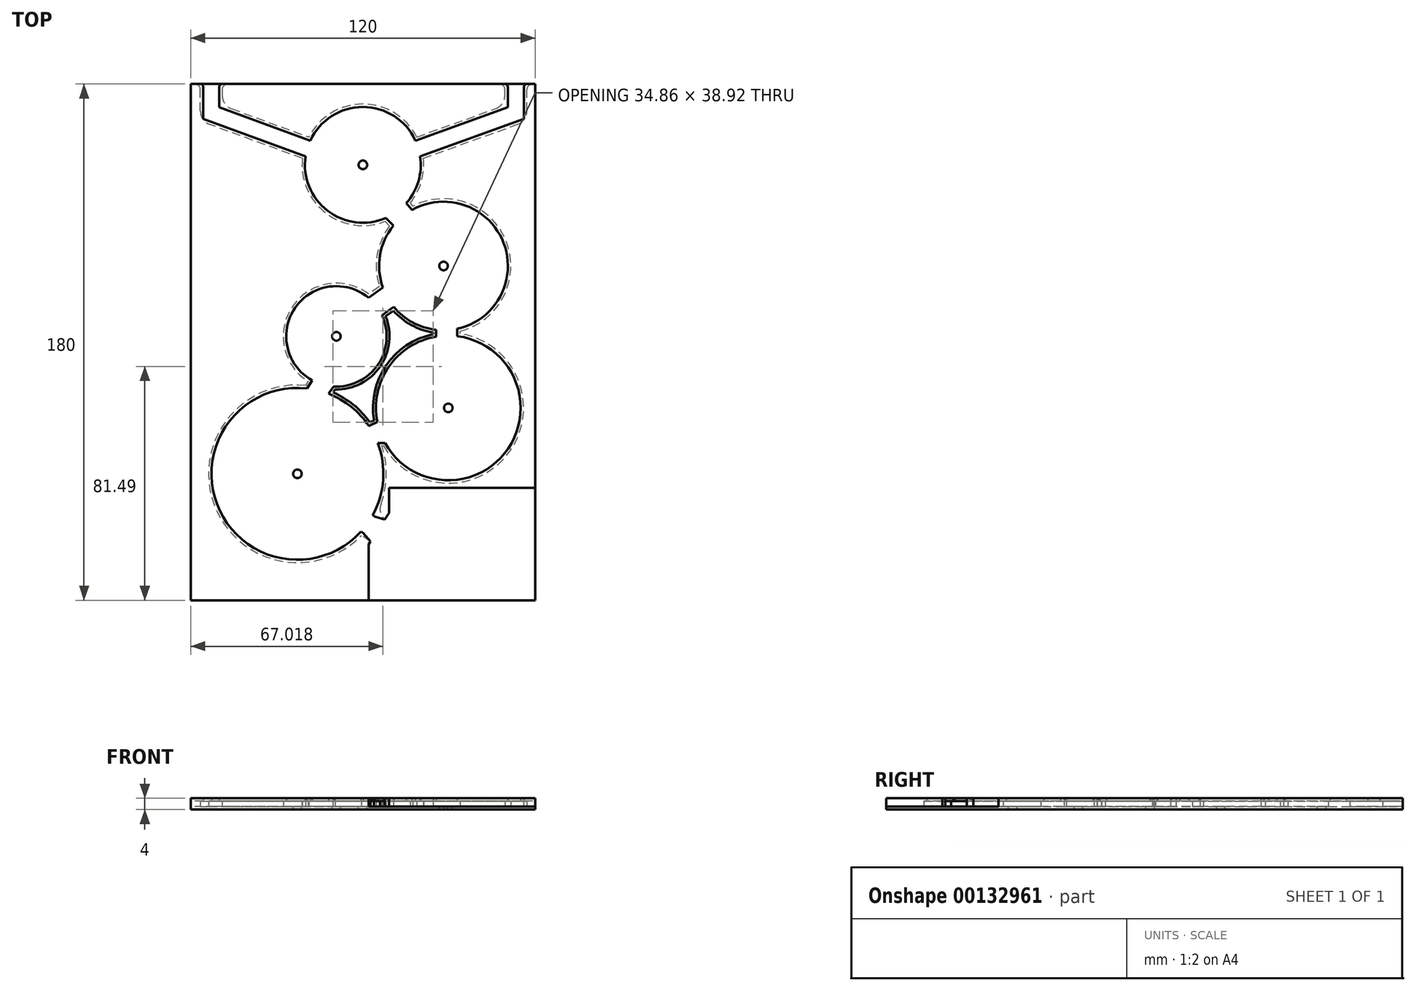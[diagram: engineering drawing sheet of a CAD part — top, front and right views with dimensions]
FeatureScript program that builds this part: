
annotation { "Feature Type Name" : "Feature", "Feature Type Description" : "" }
export const myFeature = defineFeature(function(context is Context, id is Id, definition is map)
    precondition{}
    {
        {
            var Q0;
            Q0=qCreatedBy(makeId("Top.planeOp"),FACE);
            var sketch = newSketch(context, id + "F0", { "sketchPlane" : qUnion([Q0])});
            skLineSegment(sketch, "E0.bottom", {"start": v(60, -90) * mm, "end": v(-60, -90) * mm});
            skLineSegment(sketch, "E0.top", {"start": v(60, 90) * mm, "end": v(-60, 90) * mm});
            skLineSegment(sketch, "E0.left", {"start": v(60, -90) * mm, "end": v(60, 90) * mm});
            skLineSegment(sketch, "E0.right", {"start": v(-60, -90) * mm, "end": v(-60, 90) * mm});
            skPoint(sketch, "E0.middle", {"position": v(0, 0) * mm});
            skSolve(sketch);
        }
        {
            var Q0;
            Q0 = qSketchRegion(id + "F0", true);
            extrude(context, id + "F1", {"entities" : qUnion([Q0]), "depth" : 1 * mm});
        }
        {
            var Q0;
            Q0=makeQuery(id+"F1.opExtrude","CAP_FACE",FACE,{"disambiguationData":[OSD([sQuery(id+"F0.wireOp",EDGE,"E0.bottom"),sQuery(id+"F0.wireOp",EDGE,"E0.top"),sQuery(id+"F0.wireOp",EDGE,"E0.left"),sQuery(id+"F0.wireOp",EDGE,"E0.right")])],"isStart":false});
            var sketch = newSketch(context, id + "F2", { "sketchPlane" : qUnion([Q0])});
            skArc(sketch, "E1", {"start": v(9.31, 40.56) * mm, "mid": v(4.98, 30.41) * mm, "end": v(5.77, 19.41) * mm});
            skArc(sketch, "E2", {"start": v(2, 16.73) * mm, "mid": v(-24.42, 12.56) * mm, "end": v(-19.08, -13.65) * mm});
            skArc(sketch, "E3", {"start": v(-19.98, -15.08) * mm, "mid": v(-51.81, -56.71) * mm, "end": v(-0.51, -67.4) * mm});
            skArc(sketch, "E4", {"start": v(24.45, 2.73) * mm, "mid": v(8.12, -8.13) * mm, "end": v(3.9, -27.29) * mm});
            skArc(sketch, "E5", {"start": v(16.45, 48.47) * mm, "mid": v(-12.5, 78.9) * mm, "end": v(7.75, 42.1) * mm});
            skLineSegment(sketch, "E6.bottom", {"start": v(-60, 90) * mm, "end": v(60, 90) * mm});
            skLineSegment(sketch, "E6.top", {"start": v(-60, -90) * mm, "end": v(60, -90) * mm});
            skLineSegment(sketch, "E6.left", {"start": v(-60, 90) * mm, "end": v(-60, -90) * mm});
            skLineSegment(sketch, "E6.right", {"start": v(60, 90) * mm, "end": v(60, -90) * mm});
            skLineSegment(sketch, "E7", {"start": v(7.75, 42.1) * mm, "end": v(9.31, 40.56) * mm});
            skLineSegment(sketch, "E8", {"start": v(16.45, 48.47) * mm, "end": v(17.36, 47.38) * mm});
            skLineSegment(sketch, "E9", {"start": v(5.77, 19.41) * mm, "end": v(2, 16.73) * mm});
            skLineSegment(sketch, "E10", {"start": v(10.6, 10.95) * mm, "end": v(7.9, 9.04) * mm});
            skArc(sketch, "E11.trimOffspring", {"start": v(10.6, 10.95) * mm, "mid": v(16.87, 5.97) * mm, "end": v(24.45, 3.4) * mm});
            skLineSegment(sketch, "E12", {"start": v(24.45, 2.73) * mm, "end": v(24.45, 3.4) * mm});
            skLineSegment(sketch, "E13", {"start": v(33.93, 2.94) * mm, "end": v(33.93, 3.84) * mm});
            skArc(sketch, "E14.trimOffspring", {"start": v(33.93, 3.84) * mm, "mid": v(50, 34.88) * mm, "end": v(17.36, 47.38) * mm});
            skLineSegment(sketch, "E15", {"start": v(-19.08, -13.65) * mm, "end": v(-19.98, -15.08) * mm});
            skLineSegment(sketch, "E16", {"start": v(-10.4, -17.54) * mm, "end": v(-9.65, -16.5) * mm});
            skArc(sketch, "E17.trimOffspring", {"start": v(-9.65, -16.5) * mm, "mid": v(6.03, -8.47) * mm, "end": v(7.9, 9.04) * mm});
            skLineSegment(sketch, "E18", {"start": v(2.43, -27.97) * mm, "end": v(3.9, -27.29) * mm});
            skLineSegment(sketch, "E19", {"start": v(6.58, -36.13) * mm, "end": v(7.09, -36.13) * mm});
            skArc(sketch, "E20.trimOffspring", {"start": v(7.09, -36.13) * mm, "mid": v(51.38, -37.8) * mm, "end": v(33.93, 2.94) * mm});
            skArc(sketch, "E21.trimOffspring", {"start": v(2.43, -27.97) * mm, "mid": v(-3.28, -21.88) * mm, "end": v(-10.4, -17.54) * mm});
            skLineSegment(sketch, "E22.bottom", {"start": v(60, -90) * mm, "end": v(9.07, -90) * mm});
            skLineSegment(sketch, "E22.top", {"start": v(60, -50.87) * mm, "end": v(9.07, -50.87) * mm});
            skLineSegment(sketch, "E22.left", {"start": v(60, -90) * mm, "end": v(60, -50.87) * mm});
            skLineSegment(sketch, "E23.bottom", {"start": v(1.97, -90) * mm, "end": v(9.07, -90) * mm});
            skLineSegment(sketch, "E23.left", {"start": v(1.97, -90) * mm, "end": v(1.97, -70.43) * mm});
            skLineSegment(sketch, "E24", {"start": v(1.97, -70.43) * mm, "end": v(2.62, -69.44) * mm});
            skLineSegment(sketch, "E25.trimOffspring", {"start": v(9.07, -59.55) * mm, "end": v(9.07, -50.87) * mm});
            skLineSegment(sketch, "E26", {"start": v(7.56, -61.87) * mm, "end": v(4.75, -60.04) * mm});
            skLineSegment(sketch, "E27", {"start": v(2.62, -69.44) * mm, "end": v(-0.51, -67.4) * mm});
            skLineSegment(sketch, "E28.trimOffspring", {"start": v(7.56, -61.87) * mm, "end": v(9.07, -59.55) * mm});
            skArc(sketch, "E29.trimOffspring", {"start": v(4.75, -60.04) * mm, "mid": v(8.07, -48.27) * mm, "end": v(6.58, -36.13) * mm});
            skLineSegment(sketch, "E30", {"start": v(-21.06, 64.09) * mm, "end": v(-56.61, 77.08) * mm});
            skLineSegment(sketch, "E31", {"start": v(-56.61, 77.08) * mm, "end": v(-56.61, 90) * mm});
            skLineSegment(sketch, "E32", {"start": v(-56.61, 90) * mm, "end": v(-49.03, 90) * mm});
            skLineSegment(sketch, "E33", {"start": v(-49.03, 90) * mm, "end": v(-49.03, 82.56) * mm});
            skLineSegment(sketch, "E34", {"start": v(-49.03, 82.56) * mm, "end": v(-18.82, 71.52) * mm});
            skLineSegment(sketch, "E35", {"start": v(18.82, 71.52) * mm, "end": v(49.48, 82.56) * mm});
            skLineSegment(sketch, "E36", {"start": v(49.48, 82.56) * mm, "end": v(49.48, 90) * mm});
            skLineSegment(sketch, "E37", {"start": v(21.06, 64.09) * mm, "end": v(57.14, 77.08) * mm});
            skLineSegment(sketch, "E38", {"start": v(57.14, 77.08) * mm, "end": v(57.14, 90) * mm});
            skSolve(sketch);
        }
        {
            var Q0;
            Q0=makeQuery(id+"F2.imprint","IMPRINT",FACE,{"disambiguationData":[TD([[makeQuery(id+"F2.imprint","IMPRINT",EDGE,{"derivedFrom":sQuery(id+"F2.wireOp",EDGE,"E2")}),-1.0]])]});
            var Q1;
            Q1=makeQuery(id+"F2.imprint","IMPRINT",FACE,{"disambiguationData":[TD([[makeQuery(id+"F2.imprint","IMPRINT",EDGE,{"derivedFrom":sQuery(id+"F2.wireOp",EDGE,"E4")}),-1.0]])]});
            var Q2;
            {var subQ3=sQuery(id+"F2.wireOp",EDGE,"E6.right");Q2=makeQuery(id+"F2.imprint","IMPRINT",FACE,{"disambiguationData":[TD([[makeQuery(id+"F2.imprint","IMPRINT",EDGE,{"derivedFrom":subQ3}),1.0]])]});}
            var Q3;
            {var subQ1=sQuery(id+"F2.wireOp",EDGE,"E33");Q3=makeQuery(id+"F2.imprint","IMPRINT",FACE,{"disambiguationData":[TD([[makeQuery(id+"F2.imprint","IMPRINT",EDGE,{"derivedFrom":subQ1}),1.0]])]});}
            extrude(context, id + "F3", {"entities" : qUnion([Q0, Q1, Q2, Q3]), "operationType" : NewBodyOperationType.ADD, "offsetDistance" : 25 * mm, "depth" : 2 * mm});
        }
        {
            var Q0;
            Q0=makeQuery(id+"F1.opExtrude","CAP_FACE",FACE,{"disambiguationData":[OSD([sQuery(id+"F0.wireOp",EDGE,"E0.bottom"),sQuery(id+"F0.wireOp",EDGE,"E0.top"),sQuery(id+"F0.wireOp",EDGE,"E0.left"),sQuery(id+"F0.wireOp",EDGE,"E0.right")])],"isStart":false});
            var sketch = newSketch(context, id + "F4", { "sketchPlane" : qUnion([Q0])});
            skCircle(sketch, "E39", {"center": v(0, 61.8) * mm, "radius": 1.5 * mm});
            skCircle(sketch, "E40", {"center": v(28.1, 26.55) * mm, "radius": 1.5 * mm});
            skCircle(sketch, "E41", {"center": v(-9.22, 2.01) * mm, "radius": 1.5 * mm});
            skCircle(sketch, "E42", {"center": v(29.76, -22.95) * mm, "radius": 1.5 * mm});
            skCircle(sketch, "E43", {"center": v(-22.8, -45.91) * mm, "radius": 1.5 * mm});
            skSolve(sketch);
        }
        {
            var Q0;
            Q0=makeQuery(id+"F4.imprint","IMPRINT",FACE,{"disambiguationData":[TD([[makeQuery(id+"F4.imprint","IMPRINT",EDGE,{"derivedFrom":sQuery(id+"F4.wireOp",EDGE,"E41")}),1.0]])]});
            var Q1;
            Q1=makeQuery(id+"F4.imprint","IMPRINT",FACE,{"disambiguationData":[TD([[makeQuery(id+"F4.imprint","IMPRINT",EDGE,{"derivedFrom":sQuery(id+"F4.wireOp",EDGE,"E42")}),1.0]])]});
            var Q2;
            Q2=makeQuery(id+"F4.imprint","IMPRINT",FACE,{"disambiguationData":[TD([[makeQuery(id+"F4.imprint","IMPRINT",EDGE,{"derivedFrom":sQuery(id+"F4.wireOp",EDGE,"E43")}),1.0]])]});
            var Q3;
            Q3=makeQuery(id+"F4.imprint","IMPRINT",FACE,{"disambiguationData":[TD([[makeQuery(id+"F4.imprint","IMPRINT",EDGE,{"derivedFrom":sQuery(id+"F4.wireOp",EDGE,"E40")}),1.0]])]});
            var Q4;
            Q4=makeQuery(id+"F4.imprint","IMPRINT",FACE,{"disambiguationData":[TD([[makeQuery(id+"F4.imprint","IMPRINT",EDGE,{"derivedFrom":sQuery(id+"F4.wireOp",EDGE,"E39")}),1.0]])]});
            var Q5;
            Q5=makeQuery(id+"F1.opExtrude","CAP_FACE",FACE,{"disambiguationData":[OSD([sQuery(id+"F0.wireOp",EDGE,"E0.bottom"),sQuery(id+"F0.wireOp",EDGE,"E0.top"),sQuery(id+"F0.wireOp",EDGE,"E0.left"),sQuery(id+"F0.wireOp",EDGE,"E0.right")])],"isStart":true});
            var Q6;
            Q6=makeQuery(id+"FUv2vZ3mufsg2gV_2.opPattern","COPY",FACE,{"derivedFrom":makeQuery(id+"F3.opExtrude","CAP_FACE",FACE,{"disambiguationData":[OSD([sQuery(id+"F2.wireOp",EDGE,"E5"),sQuery(id+"F2.wireOp",EDGE,"E6.bottom"),sQuery(id+"F2.wireOp",EDGE,"E33"),sQuery(id+"F2.wireOp",EDGE,"E34"),sQuery(id+"F2.wireOp",EDGE,"E35"),sQuery(id+"F2.wireOp",EDGE,"E36")])],"isStart":false}),"instanceName":"1"});
            extrude(context, id + "F5", {"entities" : qUnion([Q0, Q1, Q2, Q3, Q4]), "operationType" : NewBodyOperationType.REMOVE, "endBound" : BoundingType.UP_TO_SURFACE, "oppositeDirection" : true, "depth" : 25 * mm, "endBoundEntityFace" : qUnion([Q5]), "offsetDistance" : 25 * mm});
        }
        {
            var Q0;
            Q0=makeQuery(id+"F3.opExtrude","CAP_FACE",FACE,{"disambiguationData":[OSD([sQuery(id+"F2.wireOp",EDGE,"E5"),sQuery(id+"F2.wireOp",EDGE,"E6.bottom"),sQuery(id+"F2.wireOp",EDGE,"E33"),sQuery(id+"F2.wireOp",EDGE,"E34"),sQuery(id+"F2.wireOp",EDGE,"E35"),sQuery(id+"F2.wireOp",EDGE,"E36")])],"isStart":false});
            var sketch = newSketch(context, id + "F6", { "sketchPlane" : qUnion([Q0])});
            skLineSegment(sketch, "E44.0", {"start": v(-18.32, 70.27) * mm, "end": v(-50.03, 81.87) * mm});
            skArc(sketch, "E44.1", {"start": v(18.32, 70.28) * mm, "mid": v(0, 81.99) * mm, "end": v(-18.32, 70.27) * mm});
            skLineSegment(sketch, "E44.2", {"start": v(50.48, 81.86) * mm, "end": v(18.32, 70.28) * mm});
            skLineSegment(sketch, "E44.3", {"start": v(50.48, 89) * mm, "end": v(50.48, 81.86) * mm});
            skLineSegment(sketch, "E44.5", {"start": v(56.14, 77.79) * mm, "end": v(56.14, 89) * mm});
            skLineSegment(sketch, "E44.6", {"start": v(19.96, 64.76) * mm, "end": v(56.14, 77.79) * mm});
            skArc(sketch, "E44.7", {"start": v(15.14, 48.47) * mm, "mid": v(19.35, 56.08) * mm, "end": v(19.96, 64.76) * mm});
            skLineSegment(sketch, "E44.8", {"start": v(17.1, 46.1) * mm, "end": v(15.14, 48.47) * mm});
            skArc(sketch, "E44.9", {"start": v(32.93, 4.63) * mm, "mid": v(49.06, 34.54) * mm, "end": v(17.1, 46.1) * mm});
            skLineSegment(sketch, "E44.10", {"start": v(32.93, 2.08) * mm, "end": v(32.93, 4.63) * mm});
            skArc(sketch, "E44.11", {"start": v(-19.47, -16.14) * mm, "mid": v(-50.84, -56.46) * mm, "end": v(-0.67, -66.1) * mm});
            skLineSegment(sketch, "E44.12", {"start": v(-17.68, -13.31) * mm, "end": v(-19.47, -16.14) * mm});
            skArc(sketch, "E44.13", {"start": v(1.96, 15.48) * mm, "mid": v(-23.68, 11.88) * mm, "end": v(-17.68, -13.31) * mm});
            skLineSegment(sketch, "E44.14", {"start": v(6.96, 19.03) * mm, "end": v(1.96, 15.48) * mm});
            skArc(sketch, "E44.15", {"start": v(10.65, 40.65) * mm, "mid": v(5.98, 30.32) * mm, "end": v(6.96, 19.03) * mm});
            skLineSegment(sketch, "E44.16", {"start": v(7.98, 43.27) * mm, "end": v(10.65, 40.65) * mm});
            skLineSegment(sketch, "E44.18", {"start": v(-55.61, 89) * mm, "end": v(-55.61, 77.78) * mm});
            skLineSegment(sketch, "E44.19", {"start": v(-55.61, 77.78) * mm, "end": v(-19.96, 64.75) * mm});
            skArc(sketch, "E44.20", {"start": v(-19.96, 64.75) * mm, "mid": v(-12.3, 45.81) * mm, "end": v(7.98, 43.27) * mm});
            skLineSegment(sketch, "E44.29", {"start": v(4.17, -60.85) * mm, "end": v(3.44, -60.38) * mm});
            skArc(sketch, "E44.30", {"start": v(3.44, -60.38) * mm, "mid": v(7.1, -47.94) * mm, "end": v(5.15, -35.13) * mm});
            skLineSegment(sketch, "E44.31", {"start": v(5.15, -35.13) * mm, "end": v(7.67, -35.13) * mm});
            skLineSegment(sketch, "E44.32", {"start": v(-50.03, 81.87) * mm, "end": v(-50.03, 89) * mm});
            skArc(sketch, "E44.33", {"start": v(7.67, -35.13) * mm, "mid": v(50.63, -37.12) * mm, "end": v(32.93, 2.08) * mm});
            skPoint(sketch, "E45.0", {"position": v(7.56, -61.87) * mm});
            skPoint(sketch, "E46.0", {"position": v(2.62, -69.44) * mm});
            skLineSegment(sketch, "E47.0", {"start": v(25.45, 1.9) * mm, "end": v(25.45, 4.27) * mm});
            skArc(sketch, "E47.1", {"start": v(5.02, -27.87) * mm, "mid": v(8.96, -8.68) * mm, "end": v(25.45, 1.9) * mm});
            skArc(sketch, "E47.2", {"start": v(25.45, 4.27) * mm, "mid": v(17.34, 6.86) * mm, "end": v(10.78, 12.29) * mm});
            skLineSegment(sketch, "E47.3", {"start": v(2.09, -29.23) * mm, "end": v(5.02, -27.87) * mm});
            skLineSegment(sketch, "E47.4", {"start": v(10.78, 12.29) * mm, "end": v(6.66, 9.4) * mm});
            skArc(sketch, "E47.5", {"start": v(6.66, 9.4) * mm, "mid": v(5.29, -7.8) * mm, "end": v(-10.15, -15.47) * mm});
            skLineSegment(sketch, "E47.6", {"start": v(-10.15, -15.47) * mm, "end": v(-11.96, -17.98) * mm});
            skArc(sketch, "E47.7", {"start": v(-11.96, -17.98) * mm, "mid": v(-4.07, -22.53) * mm, "end": v(2.09, -29.23) * mm});
            skPoint(sketch, "E48.0", {"position": v(-56.61, 90) * mm});
            skPoint(sketch, "E49.0", {"position": v(57.14, 90) * mm});
            skPoint(sketch, "E50.0", {"position": v(49.48, 90) * mm});
            skLineSegment(sketch, "E51", {"start": v(2.62, -69.44) * mm, "end": v(0.07, -66.58) * mm});
            skLineSegment(sketch, "E52", {"start": v(7.56, -61.87) * mm, "end": v(4.17, -60.85) * mm});
            skLineSegment(sketch, "E53", {"start": v(-0.67, -66.1) * mm, "end": v(0.07, -66.58) * mm});
            skLineSegment(sketch, "E54.0.0", {"start": v(-21.06, 64.09) * mm, "end": v(-56.61, 77.08) * mm});
            skLineSegment(sketch, "E54.0.1", {"start": v(-56.61, 77.08) * mm, "end": v(-56.61, 90) * mm});
            skLineSegment(sketch, "E54.0.2", {"start": v(-56.61, 90) * mm, "end": v(-60, 90) * mm});
            skLineSegment(sketch, "E54.0.3", {"start": v(-60, 90) * mm, "end": v(-60, -90) * mm});
            skLineSegment(sketch, "E54.0.4", {"start": v(-60, -90) * mm, "end": v(1.97, -90) * mm});
            skLineSegment(sketch, "E54.0.5", {"start": v(1.97, -90) * mm, "end": v(1.97, -70.43) * mm});
            skLineSegment(sketch, "E54.0.6", {"start": v(1.97, -70.43) * mm, "end": v(2.62, -69.44) * mm});
            skLineSegment(sketch, "E54.0.7", {"start": v(2.62, -69.44) * mm, "end": v(-0.51, -67.4) * mm});
            skArc(sketch, "E54.0.8", {"start": v(-0.51, -67.4) * mm, "mid": v(-51.81, -56.71) * mm, "end": v(-19.98, -15.08) * mm});
            skLineSegment(sketch, "E54.0.9", {"start": v(-19.98, -15.08) * mm, "end": v(-19.08, -13.65) * mm});
            skArc(sketch, "E54.0.10", {"start": v(-19.08, -13.65) * mm, "mid": v(-24.42, 12.56) * mm, "end": v(2, 16.73) * mm});
            skLineSegment(sketch, "E54.0.11", {"start": v(2, 16.73) * mm, "end": v(5.77, 19.41) * mm});
            skArc(sketch, "E54.0.12", {"start": v(5.77, 19.41) * mm, "mid": v(4.98, 30.41) * mm, "end": v(9.31, 40.56) * mm});
            skLineSegment(sketch, "E54.0.13", {"start": v(9.31, 40.56) * mm, "end": v(7.75, 42.1) * mm});
            skArc(sketch, "E54.0.14", {"start": v(7.75, 42.1) * mm, "mid": v(-12.85, 44.97) * mm, "end": v(-21.06, 64.09) * mm});
            skLineSegment(sketch, "E55.0.0", {"start": v(57.14, 90) * mm, "end": v(57.14, 77.08) * mm});
            skLineSegment(sketch, "E55.0.1", {"start": v(57.14, 77.08) * mm, "end": v(21.06, 64.09) * mm});
            skArc(sketch, "E55.0.2", {"start": v(21.06, 64.09) * mm, "mid": v(20.31, 55.82) * mm, "end": v(16.45, 48.47) * mm});
            skLineSegment(sketch, "E55.0.3", {"start": v(16.45, 48.47) * mm, "end": v(17.36, 47.38) * mm});
            skArc(sketch, "E55.0.4", {"start": v(17.36, 47.38) * mm, "mid": v(50, 34.88) * mm, "end": v(33.93, 3.84) * mm});
            skLineSegment(sketch, "E55.0.5", {"start": v(33.93, 3.84) * mm, "end": v(33.93, 2.94) * mm});
            skArc(sketch, "E55.0.6", {"start": v(33.93, 2.94) * mm, "mid": v(51.38, -37.8) * mm, "end": v(7.09, -36.13) * mm});
            skLineSegment(sketch, "E55.0.7", {"start": v(7.09, -36.13) * mm, "end": v(6.58, -36.13) * mm});
            skArc(sketch, "E55.0.8", {"start": v(6.58, -36.13) * mm, "mid": v(8.07, -48.27) * mm, "end": v(4.75, -60.04) * mm});
            skLineSegment(sketch, "E55.0.9", {"start": v(4.75, -60.04) * mm, "end": v(7.56, -61.87) * mm});
            skLineSegment(sketch, "E55.0.10", {"start": v(7.56, -61.87) * mm, "end": v(9.07, -59.55) * mm});
            skLineSegment(sketch, "E55.0.11", {"start": v(9.07, -59.55) * mm, "end": v(9.07, -50.87) * mm});
            skLineSegment(sketch, "E55.0.12", {"start": v(9.07, -50.87) * mm, "end": v(60, -50.87) * mm});
            skLineSegment(sketch, "E55.0.13", {"start": v(60, -50.87) * mm, "end": v(60, 90) * mm});
            skLineSegment(sketch, "E55.0.14", {"start": v(60, 90) * mm, "end": v(57.14, 90) * mm});
            skArc(sketch, "E56.0.0", {"start": v(24.45, 3.4) * mm, "mid": v(16.87, 5.97) * mm, "end": v(10.6, 10.95) * mm});
            skLineSegment(sketch, "E56.0.1", {"start": v(10.6, 10.95) * mm, "end": v(7.9, 9.04) * mm});
            skArc(sketch, "E56.0.2", {"start": v(7.9, 9.04) * mm, "mid": v(6.03, -8.47) * mm, "end": v(-9.65, -16.5) * mm});
            skLineSegment(sketch, "E56.0.3", {"start": v(-9.65, -16.5) * mm, "end": v(-10.4, -17.54) * mm});
            skArc(sketch, "E56.0.4", {"start": v(-10.4, -17.54) * mm, "mid": v(-3.28, -21.88) * mm, "end": v(2.43, -27.97) * mm});
            skLineSegment(sketch, "E56.0.5", {"start": v(2.43, -27.97) * mm, "end": v(3.9, -27.29) * mm});
            skArc(sketch, "E56.0.6", {"start": v(3.9, -27.29) * mm, "mid": v(8.12, -8.13) * mm, "end": v(24.45, 2.73) * mm});
            skLineSegment(sketch, "E56.0.7", {"start": v(24.45, 2.73) * mm, "end": v(24.45, 3.4) * mm});
            skLineSegment(sketch, "E57.0", {"start": v(57.14, 90) * mm, "end": v(56.14, 90) * mm});
            skLineSegment(sketch, "E58.0", {"start": v(-49.03, 90) * mm, "end": v(-50.03, 90) * mm});
            skLineSegment(sketch, "E59", {"start": v(-55.61, 89) * mm, "end": v(-55.61, 90) * mm});
            skLineSegment(sketch, "E60", {"start": v(-50.03, 89) * mm, "end": v(-50.03, 90) * mm});
            skLineSegment(sketch, "E61", {"start": v(50.48, 89) * mm, "end": v(50.48, 90) * mm});
            skLineSegment(sketch, "E62", {"start": v(56.14, 89) * mm, "end": v(56.14, 90) * mm});
            skLineSegment(sketch, "E63.trimOffspring", {"start": v(50.48, 90) * mm, "end": v(49.48, 90) * mm});
            skLineSegment(sketch, "E64.trimOffspring", {"start": v(-55.61, 90) * mm, "end": v(-56.61, 90) * mm});
            skSolve(sketch);
        }
        {
            var Q0;
            Q0=makeQuery(id+"F6.imprint","IMPRINT",FACE,{"disambiguationData":[TD([[makeQuery(id+"F6.imprint","IMPRINT",EDGE,{"derivedFrom":sQuery(id+"F6.wireOp",EDGE,"E44.0")}),-1.0]])]});
            var Q1;
            Q1=makeQuery(id+"F6.imprint","IMPRINT",FACE,{"disambiguationData":[TD([[makeQuery(id+"F6.imprint","IMPRINT",EDGE,{"derivedFrom":sQuery(id+"F6.wireOp",EDGE,"E44.11")}),-1.0]])]});
            var Q2;
            Q2=makeQuery(id+"F6.imprint","IMPRINT",FACE,{"disambiguationData":[TD([[makeQuery(id+"F6.imprint","IMPRINT",EDGE,{"derivedFrom":sQuery(id+"F6.wireOp",EDGE,"E44.5")}),-1.0]])]});
            var Q3;
            Q3=makeQuery(id+"F6.imprint","IMPRINT",FACE,{"disambiguationData":[TD([[makeQuery(id+"F6.imprint","IMPRINT",EDGE,{"derivedFrom":sQuery(id+"F6.wireOp",EDGE,"E47.0")}),1.0]])]});
            var Q4;
            {var subQ1=sQuery(id+"F2.wireOp",EDGE,"E33");Q4=makeQuery(id+"F6.imprint","IMPRINT",FACE,{"disambiguationData":[TD([[makeQuery(id+"F6.imprint","IMPRINT",EDGE,{"derivedFrom":makeQuery(id+"F3.opExtrude","CAP_EDGE",EDGE,{"disambiguationData":[OSD([subQ1])],"isStart":false})}),1.0]])]});}
            var Q5;
            Q5=makeQuery(id+"F6.imprint","IMPRINT",FACE,{"disambiguationData":[TD([[makeQuery(id+"F6.imprint","IMPRINT",EDGE,{"derivedFrom":sQuery(id+"F6.wireOp",EDGE,"E55.0.0")}),1.0]])]});
            var Q6;
            Q6=makeQuery(id+"F6.imprint","IMPRINT",FACE,{"disambiguationData":[TD([[makeQuery(id+"F6.imprint","IMPRINT",EDGE,{"derivedFrom":sQuery(id+"F6.wireOp",EDGE,"E54.0.0")}),1.0]])]});
            var Q7;
            Q7=makeQuery(id+"F6.imprint","IMPRINT",FACE,{"disambiguationData":[TD([[makeQuery(id+"F6.imprint","IMPRINT",EDGE,{"derivedFrom":sQuery(id+"F6.wireOp",EDGE,"E56.0.0")}),1.0]])]});
            extrude(context, id + "F7", {"entities" : qUnion([Q0, Q1, Q2, Q3, Q4, Q5, Q6, Q7]), "operationType" : NewBodyOperationType.ADD, "depth" : 1 * mm, "offsetDistance" : 25 * mm});
        }
        {
            var Q0;
            Q0=makeQuery(id+"F7.opExtrude","SWEPT_EDGE",EDGE,{"disambiguationData":[OSD([sQuery(id+"F6.wireOp",EDGE,"E58.0"),sQuery(id+"F6.wireOp",EDGE,"E60")])]});
            var Q1;
            Q1=makeQuery(id+"F7.opExtrude","SWEPT_EDGE",EDGE,{"disambiguationData":[OSD([sQuery(id+"F6.wireOp",EDGE,"E59"),sQuery(id+"F6.wireOp",EDGE,"E64.trimOffspring")])]});
            var Q2;
            Q2=makeQuery(id+"F7.opExtrude","SWEPT_EDGE",EDGE,{"disambiguationData":[OSD([sQuery(id+"F6.wireOp",EDGE,"E57.0"),sQuery(id+"F6.wireOp",EDGE,"E62")])]});
            var Q3;
            Q3=makeQuery(id+"F7.opExtrude","SWEPT_EDGE",EDGE,{"disambiguationData":[OSD([sQuery(id+"F6.wireOp",EDGE,"E61"),sQuery(id+"F6.wireOp",EDGE,"E63.trimOffspring")])]});
            fillet(context, id + "F8", {"entities" : qUnion([Q0, Q1, Q2, Q3]), "radius" : 1 * mm, "tangentPropagation" : true, "allowEdgeOverflow" : false});
        }
        {
            var Q0;
            Q0=makeQuery(id+"F3.opExtrude","SWEPT_EDGE",EDGE,{"disambiguationData":[OSD([sQuery(id+"F2.wireOp",EDGE,"E6.bottom"),sQuery(id+"F2.wireOp",EDGE,"E31"),sQuery(id+"F2.wireOp",EDGE,"E32")])]});
            var Q1;
            Q1=makeQuery(id+"F3.opExtrude","SWEPT_EDGE",EDGE,{"disambiguationData":[OSD([sQuery(id+"F2.wireOp",EDGE,"E6.bottom"),sQuery(id+"F2.wireOp",EDGE,"E32"),sQuery(id+"F2.wireOp",EDGE,"E33")])]});
            var Q2;
            Q2=makeQuery(id+"F3.opExtrude","SWEPT_EDGE",EDGE,{"disambiguationData":[OSD([sQuery(id+"F2.wireOp",EDGE,"E6.bottom"),sQuery(id+"F2.wireOp",EDGE,"E36")])]});
            var Q3;
            Q3=makeQuery(id+"F3.opExtrude","SWEPT_EDGE",EDGE,{"disambiguationData":[OSD([sQuery(id+"F2.wireOp",EDGE,"E6.bottom"),sQuery(id+"F2.wireOp",EDGE,"E38")])]});
            fillet(context, id + "F9", {"entities" : qUnion([Q0, Q1, Q2, Q3]), "radius" : 2 * mm, "tangentPropagation" : true, "allowEdgeOverflow" : false});
        }
        {
            var Q0;
            Q0=makeQuery(id+"F3.opExtrude","SWEPT_EDGE",EDGE,{"disambiguationData":[OSD([sQuery(id+"F2.wireOp",EDGE,"E33"),sQuery(id+"F2.wireOp",EDGE,"E34")])]});
            var Q1;
            Q1=makeQuery(id+"F3.opExtrude","SWEPT_EDGE",EDGE,{"disambiguationData":[OSD([sQuery(id+"F2.wireOp",EDGE,"E30"),sQuery(id+"F2.wireOp",EDGE,"E31")])]});
            var Q2;
            Q2=makeQuery(id+"F3.opExtrude","SWEPT_EDGE",EDGE,{"disambiguationData":[OSD([sQuery(id+"F2.wireOp",EDGE,"E37"),sQuery(id+"F2.wireOp",EDGE,"E38")])]});
            var Q3;
            Q3=makeQuery(id+"F3.opExtrude","SWEPT_EDGE",EDGE,{"disambiguationData":[OSD([sQuery(id+"F2.wireOp",EDGE,"E35"),sQuery(id+"F2.wireOp",EDGE,"E36")])]});
            var Q4;
            Q4=makeQuery(id+"F3.opExtrude","SWEPT_EDGE",EDGE,{"disambiguationData":[OSD([sQuery(id+"F2.wireOp",EDGE,"E26"),sQuery(id+"F2.wireOp",EDGE,"E29.trimOffspring")])]});
            fillet(context, id + "F10", {"entities" : qUnion([Q0, Q1, Q2, Q3, Q4]), "radius" : 5 * mm, "tangentPropagation" : true, "allowEdgeOverflow" : false});
        }
    });
